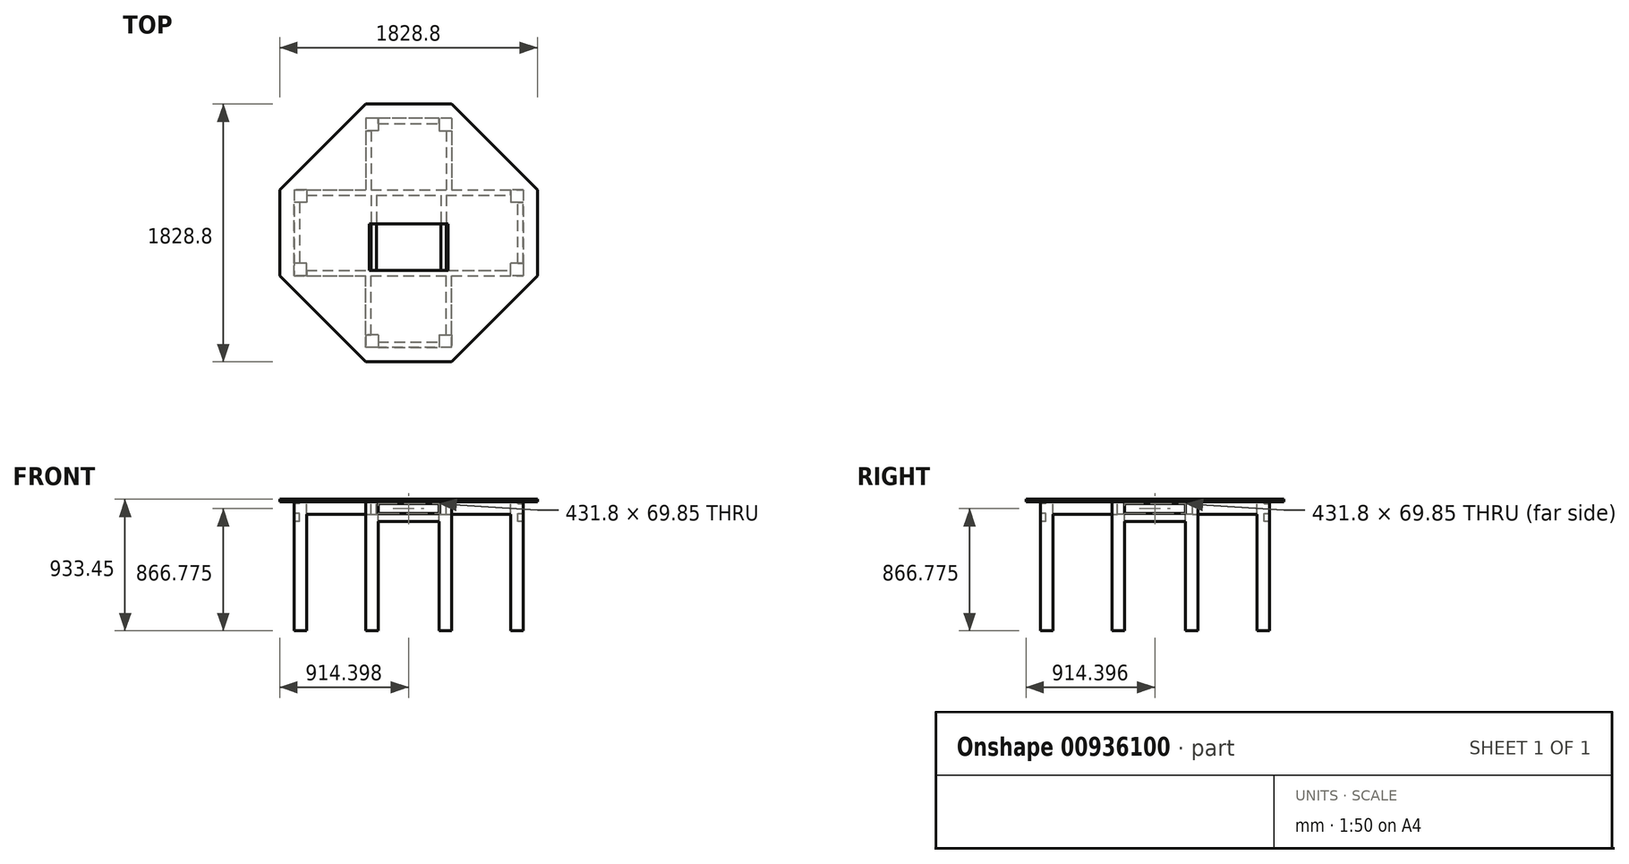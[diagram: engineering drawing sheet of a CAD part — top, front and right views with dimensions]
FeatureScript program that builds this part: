
annotation { "Feature Type Name" : "Feature", "Feature Type Description" : "" }
export const myFeature = defineFeature(function(context is Context, id is Id, definition is map)
    precondition{}
    {
        {
            var Q0;
            Q0=qCreatedBy(makeId("Top.planeOp"),FACE);
            var sketch = newSketch(context, id + "F0", { "sketchPlane" : qUnion([Q0])});
            skLineSegment(sketch, "E0.bottom", {"start": v(-298, -538.32) * mm, "end": v(311.6, -538.32) * mm});
            skLineSegment(sketch, "E0.top", {"start": v(-298, 1290.48) * mm, "end": v(311.6, 1290.48) * mm});
            skLineSegment(sketch, "E0.left", {"start": v(-907.6, 71.28) * mm, "end": v(-907.6, 680.88) * mm});
            skLineSegment(sketch, "E0.right", {"start": v(921.2, 71.28) * mm, "end": v(921.2, 680.88) * mm});
            skLineSegment(sketch, "E1", {"start": v(-298, -538.32) * mm, "end": v(-907.6, 71.28) * mm});
            skLineSegment(sketch, "E2", {"start": v(-907.6, 680.88) * mm, "end": v(-298, 1290.48) * mm});
            skLineSegment(sketch, "E3", {"start": v(921.2, 680.88) * mm, "end": v(311.6, 1290.48) * mm});
            skLineSegment(sketch, "E4", {"start": v(921.2, 71.28) * mm, "end": v(311.6, -538.32) * mm});
            skLineSegment(sketch, "E5.bottom", {"start": v(-272.6, 109.38) * mm, "end": v(286.2, 109.38) * mm});
            skLineSegment(sketch, "E5.top", {"start": v(-272.6, 439.58) * mm, "end": v(286.2, 439.58) * mm});
            skLineSegment(sketch, "E5.left", {"start": v(-272.6, 109.38) * mm, "end": v(-272.6, 439.58) * mm});
            skLineSegment(sketch, "E5.right", {"start": v(286.2, 109.38) * mm, "end": v(286.2, 439.58) * mm});
            skSolve(sketch);
        }
        {
            var Q0;
            Q0=makeQuery(id+"F0.imprint","IMPRINT",FACE,{"disambiguationData":[TD([[makeQuery(id+"F0.imprint","IMPRINT",EDGE,{"derivedFrom":sQuery(id+"F0.wireOp",EDGE,"E0.bottom")}),1.0]])]});
            extrude(context, id + "F1", {"entities" : qUnion([Q0]), "depth" : 19.05 * mm, "offsetDistance" : 25.4 * mm});
        }
        {
            var Q0;
            Q0=makeQuery(id+"F1.opExtrude","CAP_FACE",FACE,{"disambiguationData":[OSD([sQuery(id+"F0.wireOp",EDGE,"E0.bottom"),sQuery(id+"F0.wireOp",EDGE,"E0.top"),sQuery(id+"F0.wireOp",EDGE,"E0.left"),sQuery(id+"F0.wireOp",EDGE,"E0.right"),sQuery(id+"F0.wireOp",EDGE,"E1"),sQuery(id+"F0.wireOp",EDGE,"E2"),sQuery(id+"F0.wireOp",EDGE,"E3"),sQuery(id+"F0.wireOp",EDGE,"E4"),sQuery(id+"F0.wireOp",EDGE,"E5.bottom"),sQuery(id+"F0.wireOp",EDGE,"E5.top"),sQuery(id+"F0.wireOp",EDGE,"E5.left"),sQuery(id+"F0.wireOp",EDGE,"E5.right")])],"isStart":true});
            var sketch = newSketch(context, id + "F2", { "sketchPlane" : qUnion([Q0])});
            skLineSegment(sketch, "E6.bottom", {"start": v(-806, -680.88) * mm, "end": v(-717.1, -680.88) * mm});
            skLineSegment(sketch, "E6.top", {"start": v(-806, -591.98) * mm, "end": v(-717.1, -591.98) * mm});
            skLineSegment(sketch, "E6.left", {"start": v(-806, -680.88) * mm, "end": v(-806, -591.98) * mm});
            skLineSegment(sketch, "E6.right", {"start": v(-717.1, -680.88) * mm, "end": v(-717.1, -591.98) * mm});
            skLineSegment(sketch, "E7.bottom", {"start": v(-806, -160.18) * mm, "end": v(-717.1, -160.18) * mm});
            skLineSegment(sketch, "E7.top", {"start": v(-806, -71.28) * mm, "end": v(-717.1, -71.28) * mm});
            skLineSegment(sketch, "E7.left", {"start": v(-806, -160.18) * mm, "end": v(-806, -71.28) * mm});
            skLineSegment(sketch, "E7.right", {"start": v(-717.1, -160.18) * mm, "end": v(-717.1, -71.28) * mm});
            skLineSegment(sketch, "E8.bottom", {"start": v(-298, 436.72) * mm, "end": v(-209.1, 436.72) * mm});
            skLineSegment(sketch, "E8.top", {"start": v(-298, 347.82) * mm, "end": v(-209.1, 347.82) * mm});
            skLineSegment(sketch, "E8.left", {"start": v(-298, 436.72) * mm, "end": v(-298, 347.82) * mm});
            skLineSegment(sketch, "E8.right", {"start": v(-209.1, 436.72) * mm, "end": v(-209.1, 347.82) * mm});
            skLineSegment(sketch, "E9.bottom", {"start": v(222.7, 436.72) * mm, "end": v(311.6, 436.72) * mm});
            skLineSegment(sketch, "E9.top", {"start": v(222.7, 347.82) * mm, "end": v(311.6, 347.82) * mm});
            skLineSegment(sketch, "E9.left", {"start": v(222.7, 436.72) * mm, "end": v(222.7, 347.82) * mm});
            skLineSegment(sketch, "E9.right", {"start": v(311.6, 436.72) * mm, "end": v(311.6, 347.82) * mm});
            skLineSegment(sketch, "E10.bottom", {"start": v(730.7, -71.28) * mm, "end": v(819.6, -71.28) * mm});
            skLineSegment(sketch, "E10.top", {"start": v(730.7, -160.18) * mm, "end": v(819.6, -160.18) * mm});
            skLineSegment(sketch, "E10.left", {"start": v(730.7, -71.28) * mm, "end": v(730.7, -160.18) * mm});
            skLineSegment(sketch, "E10.right", {"start": v(819.6, -71.28) * mm, "end": v(819.6, -160.18) * mm});
            skPoint(sketch, "E11.firstSnap0", {"position": v(730.7, -115.73) * mm});
            skLineSegment(sketch, "E11.bottom", {"start": v(730.7, -591.98) * mm, "end": v(819.6, -591.98) * mm});
            skLineSegment(sketch, "E11.top", {"start": v(730.7, -680.88) * mm, "end": v(819.6, -680.88) * mm});
            skLineSegment(sketch, "E11.left", {"start": v(730.7, -591.98) * mm, "end": v(730.7, -680.88) * mm});
            skLineSegment(sketch, "E11.right", {"start": v(819.6, -591.98) * mm, "end": v(819.6, -680.88) * mm});
            skLineSegment(sketch, "E12.bottom", {"start": v(222.7, -1099.98) * mm, "end": v(311.6, -1099.98) * mm});
            skLineSegment(sketch, "E12.top", {"start": v(222.7, -1188.88) * mm, "end": v(311.6, -1188.88) * mm});
            skLineSegment(sketch, "E12.left", {"start": v(222.7, -1099.98) * mm, "end": v(222.7, -1188.88) * mm});
            skLineSegment(sketch, "E12.right", {"start": v(311.6, -1099.98) * mm, "end": v(311.6, -1188.88) * mm});
            skLineSegment(sketch, "E13.bottom", {"start": v(-298, -1099.98) * mm, "end": v(-209.1, -1099.98) * mm});
            skLineSegment(sketch, "E13.top", {"start": v(-298, -1188.88) * mm, "end": v(-209.1, -1188.88) * mm});
            skLineSegment(sketch, "E13.left", {"start": v(-298, -1099.98) * mm, "end": v(-298, -1188.88) * mm});
            skLineSegment(sketch, "E13.right", {"start": v(-209.1, -1099.98) * mm, "end": v(-209.1, -1188.88) * mm});
            skLineSegment(sketch, "E14.bottom", {"start": v(-209.1, 436.72) * mm, "end": v(222.7, 436.72) * mm});
            skLineSegment(sketch, "E14.top", {"start": v(-209.1, 398.62) * mm, "end": v(222.7, 398.62) * mm});
            skLineSegment(sketch, "E14.left", {"start": v(-209.1, 436.72) * mm, "end": v(-209.1, 398.62) * mm});
            skLineSegment(sketch, "E14.right", {"start": v(222.7, 436.72) * mm, "end": v(222.7, 398.62) * mm});
            skLineSegment(sketch, "E15.bottom", {"start": v(-806, -160.18) * mm, "end": v(-767.9, -160.18) * mm});
            skLineSegment(sketch, "E15.top", {"start": v(-806, -591.98) * mm, "end": v(-767.9, -591.98) * mm});
            skLineSegment(sketch, "E15.left", {"start": v(-806, -160.18) * mm, "end": v(-806, -591.98) * mm});
            skLineSegment(sketch, "E15.right", {"start": v(-767.9, -160.18) * mm, "end": v(-767.9, -591.98) * mm});
            skLineSegment(sketch, "E16.bottom", {"start": v(-209.1, -1188.88) * mm, "end": v(222.7, -1188.88) * mm});
            skLineSegment(sketch, "E16.top", {"start": v(-209.1, -1150.78) * mm, "end": v(222.7, -1150.78) * mm});
            skLineSegment(sketch, "E16.left", {"start": v(-209.1, -1188.88) * mm, "end": v(-209.1, -1150.78) * mm});
            skLineSegment(sketch, "E16.right", {"start": v(222.7, -1188.88) * mm, "end": v(222.7, -1150.78) * mm});
            skLineSegment(sketch, "E17.bottom", {"start": v(819.6, -160.18) * mm, "end": v(781.5, -160.18) * mm});
            skLineSegment(sketch, "E17.top", {"start": v(819.6, -591.98) * mm, "end": v(781.5, -591.98) * mm});
            skLineSegment(sketch, "E17.left", {"start": v(819.6, -160.18) * mm, "end": v(819.6, -591.98) * mm});
            skLineSegment(sketch, "E17.right", {"start": v(781.5, -160.18) * mm, "end": v(781.5, -591.98) * mm});
            skLineSegment(sketch, "E18.bottom", {"start": v(-717.1, -71.28) * mm, "end": v(730.7, -71.28) * mm});
            skLineSegment(sketch, "E18.top", {"start": v(-717.1, -109.38) * mm, "end": v(730.7, -109.38) * mm});
            skLineSegment(sketch, "E18.left", {"start": v(-717.1, -71.28) * mm, "end": v(-717.1, -109.38) * mm});
            skLineSegment(sketch, "E18.right", {"start": v(730.7, -71.28) * mm, "end": v(730.7, -109.38) * mm});
            skLineSegment(sketch, "E19.bottom", {"start": v(-717.1, -680.88) * mm, "end": v(730.7, -680.88) * mm});
            skLineSegment(sketch, "E19.top", {"start": v(-717.1, -642.78) * mm, "end": v(730.7, -642.78) * mm});
            skLineSegment(sketch, "E19.left", {"start": v(-717.1, -680.88) * mm, "end": v(-717.1, -642.78) * mm});
            skLineSegment(sketch, "E19.right", {"start": v(730.7, -680.88) * mm, "end": v(730.7, -642.78) * mm});
            skLineSegment(sketch, "E20.bottom", {"start": v(311.6, 347.82) * mm, "end": v(273.5, 347.82) * mm});
            skLineSegment(sketch, "E20.top", {"start": v(311.6, -71.28) * mm, "end": v(273.5, -71.28) * mm});
            skLineSegment(sketch, "E20.left", {"start": v(311.6, 347.82) * mm, "end": v(311.6, -71.28) * mm});
            skLineSegment(sketch, "E20.right", {"start": v(273.5, 347.82) * mm, "end": v(273.5, -71.28) * mm});
            skLineSegment(sketch, "E21.bottom", {"start": v(-298, 347.82) * mm, "end": v(-259.9, 347.82) * mm});
            skLineSegment(sketch, "E21.top", {"start": v(-298, -71.28) * mm, "end": v(-259.9, -71.28) * mm});
            skLineSegment(sketch, "E21.left", {"start": v(-298, 347.82) * mm, "end": v(-298, -71.28) * mm});
            skLineSegment(sketch, "E21.right", {"start": v(-259.9, 347.82) * mm, "end": v(-259.9, -71.28) * mm});
            skLineSegment(sketch, "E22.bottom", {"start": v(-298, -1099.98) * mm, "end": v(-259.9, -1099.98) * mm});
            skLineSegment(sketch, "E22.top", {"start": v(-298, -680.88) * mm, "end": v(-259.9, -680.88) * mm});
            skLineSegment(sketch, "E22.left", {"start": v(-298, -1099.98) * mm, "end": v(-298, -680.88) * mm});
            skLineSegment(sketch, "E22.right", {"start": v(-259.9, -1099.98) * mm, "end": v(-259.9, -680.88) * mm});
            skLineSegment(sketch, "E23.bottom", {"start": v(311.6, -1099.98) * mm, "end": v(273.5, -1099.98) * mm});
            skLineSegment(sketch, "E23.top", {"start": v(311.6, -680.88) * mm, "end": v(273.5, -680.88) * mm});
            skLineSegment(sketch, "E23.left", {"start": v(311.6, -1099.98) * mm, "end": v(311.6, -680.88) * mm});
            skLineSegment(sketch, "E23.right", {"start": v(273.5, -1099.98) * mm, "end": v(273.5, -680.88) * mm});
            skLineSegment(sketch, "E24.bottom", {"start": v(273.5, -642.78) * mm, "end": v(235.4, -642.78) * mm});
            skLineSegment(sketch, "E24.top", {"start": v(273.5, -109.38) * mm, "end": v(235.4, -109.38) * mm});
            skLineSegment(sketch, "E24.left", {"start": v(273.5, -642.78) * mm, "end": v(273.5, -109.38) * mm});
            skLineSegment(sketch, "E24.right", {"start": v(235.4, -642.78) * mm, "end": v(235.4, -109.38) * mm});
            skLineSegment(sketch, "E25.bottom", {"start": v(-259.9, -642.78) * mm, "end": v(-221.8, -642.78) * mm});
            skLineSegment(sketch, "E25.top", {"start": v(-259.9, -109.38) * mm, "end": v(-221.8, -109.38) * mm});
            skLineSegment(sketch, "E25.left", {"start": v(-259.9, -642.78) * mm, "end": v(-259.9, -109.38) * mm});
            skLineSegment(sketch, "E25.right", {"start": v(-221.8, -642.78) * mm, "end": v(-221.8, -109.38) * mm});
            skSolve(sketch);
        }
        {
            var Q0;
            {var subQ2=sQuery(id+"F2.wireOp",EDGE,"E22.left");Q0=makeQuery(id+"F2.imprint","IMPRINT",FACE,{"disambiguationData":[TD([[makeQuery(id+"F2.imprint","IMPRINT",EDGE,{"derivedFrom":subQ2}),-1.0]])]});}
            var Q1;
            {var subQ0=sQuery(id+"F2.wireOp",EDGE,"E23.left");Q1=makeQuery(id+"F2.imprint","IMPRINT",FACE,{"disambiguationData":[TD([[makeQuery(id+"F2.imprint","IMPRINT",EDGE,{"derivedFrom":subQ0}),1.0]])]});}
            var Q2;
            {var subQ7=sQuery(id+"F2.wireOp",EDGE,"E19.bottom");var subQ14=makeQuery(id+"F2.imprint","INTERSECT",VERTEX,{"derivedFrom":[subQ7,sQuery(id+"F2.wireOp",EDGE,"E22.right")]});Q2=makeQuery(id+"F2.imprint","IMPRINT",FACE,{"disambiguationData":[TD([[makeQuery(id+"F2.imprint","IMPRINT",EDGE,{"disambiguationData":[TD([[subQ14,-1.0]])],"derivedFrom":subQ7}),1.0]])]});}
            var Q3;
            {var subQ0=sQuery(id+"F2.wireOp",EDGE,"E25.right");var subQ1=sQuery(id+"F2.wireOp",EDGE,"E19.top");var subQ2=makeQuery(id+"F2.imprint","INTERSECT",VERTEX,{"derivedFrom":[subQ1,subQ0]});Q3=makeQuery(id+"F2.imprint","IMPRINT",FACE,{"disambiguationData":[TD([[makeQuery(id+"F2.imprint","IMPRINT",EDGE,{"disambiguationData":[TD([[subQ2,1.0]])],"derivedFrom":subQ1}),1.0]])]});}
            var Q4;
            {var subQ4=sQuery(id+"F2.wireOp",EDGE,"E18.bottom");var subQ7=makeQuery(id+"F2.imprint","INTERSECT",VERTEX,{"derivedFrom":[subQ4,sQuery(id+"F2.wireOp",EDGE,"E21.right")]});Q4=makeQuery(id+"F2.imprint","IMPRINT",FACE,{"disambiguationData":[TD([[makeQuery(id+"F2.imprint","IMPRINT",EDGE,{"disambiguationData":[TD([[subQ7,-1.0]])],"derivedFrom":subQ4}),-1.0]])]});}
            var Q5;
            {var subQ2=sQuery(id+"F2.wireOp",EDGE,"E21.left");Q5=makeQuery(id+"F2.imprint","IMPRINT",FACE,{"disambiguationData":[TD([[makeQuery(id+"F2.imprint","IMPRINT",EDGE,{"derivedFrom":subQ2}),1.0]])]});}
            var Q6;
            {var subQ0=sQuery(id+"F2.wireOp",EDGE,"E20.left");Q6=makeQuery(id+"F2.imprint","IMPRINT",FACE,{"disambiguationData":[TD([[makeQuery(id+"F2.imprint","IMPRINT",EDGE,{"derivedFrom":subQ0}),-1.0]])]});}
            var Q7;
            {var subQ0=sQuery(id+"F2.wireOp",EDGE,"E24.left");var subQ1=sQuery(id+"F2.wireOp",EDGE,"E19.top");var subQ2=makeQuery(id+"F2.imprint","INTERSECT",VERTEX,{"derivedFrom":[subQ1,subQ0]});Q7=makeQuery(id+"F2.imprint","IMPRINT",FACE,{"disambiguationData":[TD([[makeQuery(id+"F2.imprint","IMPRINT",EDGE,{"disambiguationData":[TD([[subQ2,1.0]])],"derivedFrom":subQ1}),1.0]])]});}
            var Q8;
            {var subQ0=sQuery(id+"F2.wireOp",EDGE,"E25.left");var subQ1=sQuery(id+"F2.wireOp",EDGE,"E18.top");var subQ2=makeQuery(id+"F2.imprint","INTERSECT",VERTEX,{"derivedFrom":[subQ1,subQ0]});Q8=makeQuery(id+"F2.imprint","IMPRINT",FACE,{"disambiguationData":[TD([[makeQuery(id+"F2.imprint","IMPRINT",EDGE,{"disambiguationData":[TD([[subQ2,-1.0]])],"derivedFrom":subQ1}),-1.0]])]});}
            var Q9;
            {var subQ0=sQuery(id+"F2.wireOp",EDGE,"E24.left");var subQ1=sQuery(id+"F2.wireOp",EDGE,"E18.top");var subQ2=makeQuery(id+"F2.imprint","INTERSECT",VERTEX,{"derivedFrom":[subQ1,subQ0]});Q9=makeQuery(id+"F2.imprint","IMPRINT",FACE,{"disambiguationData":[TD([[makeQuery(id+"F2.imprint","IMPRINT",EDGE,{"disambiguationData":[TD([[subQ2,1.0]])],"derivedFrom":subQ1}),-1.0]])]});}
            extrude(context, id + "F3", {"entities" : qUnion([Q0, Q1, Q2, Q3, Q4, Q5, Q6, Q7, Q8, Q9]), "operationType" : NewBodyOperationType.ADD, "depth" : 88.9 * mm, "offsetDistance" : 25.4 * mm});
        }
        {
            var Q0;
            {var subQ5=sQuery(id+"F0.wireOp",EDGE,"E5.right");var subQ8=sQuery(id+"F0.wireOp",EDGE,"E5.left");var subQ12=sQuery(id+"F0.wireOp",EDGE,"E0.left");var subQ14=sQuery(id+"F0.wireOp",EDGE,"E0.top");var subQ30=sQuery(id+"F0.wireOp",EDGE,"E0.right");var subQ31=sQuery(id+"F0.wireOp",EDGE,"E0.bottom");var subQ34=sQuery(id+"F0.wireOp",EDGE,"E5.top");var subQ35=sQuery(id+"F0.wireOp",EDGE,"E1");var subQ37=sQuery(id+"F0.wireOp",EDGE,"E2");var subQ38=sQuery(id+"F0.wireOp",EDGE,"E3");var subQ41=sQuery(id+"F0.wireOp",EDGE,"E4");var subQ42=sQuery(id+"F0.wireOp",EDGE,"E5.bottom");Q0=makeQuery(id+"F3.boolean.opBoolean","SPLIT",FACE,{"disambiguationData":[TD([makeQuery(id+"F1.opExtrude","SWEPT_FACE",FACE,{"disambiguationData":[OSD([subQ31])]})])],"derivedFrom":makeQuery(id+"F1.opExtrude","CAP_FACE",FACE,{"disambiguationData":[OSD([subQ31,subQ14,subQ12,subQ30,subQ35,subQ37,subQ38,subQ41,subQ42,subQ34,subQ8,subQ5])],"isStart":true})});}
            var sketch = newSketch(context, id + "F4", { "sketchPlane" : qUnion([Q0])});
            skLineSegment(sketch, "E26.bottom", {"start": v(819.6, -680.88) * mm, "end": v(730.7, -680.88) * mm});
            skLineSegment(sketch, "E26.top", {"start": v(819.6, -591.98) * mm, "end": v(730.7, -591.98) * mm});
            skLineSegment(sketch, "E26.left", {"start": v(819.6, -680.88) * mm, "end": v(819.6, -591.98) * mm});
            skLineSegment(sketch, "E26.right", {"start": v(730.7, -680.88) * mm, "end": v(730.7, -591.98) * mm});
            skLineSegment(sketch, "E27.bottom", {"start": v(819.6, -160.18) * mm, "end": v(730.7, -160.18) * mm});
            skLineSegment(sketch, "E27.top", {"start": v(819.6, -71.28) * mm, "end": v(730.7, -71.28) * mm});
            skLineSegment(sketch, "E27.left", {"start": v(819.6, -160.18) * mm, "end": v(819.6, -71.28) * mm});
            skLineSegment(sketch, "E27.right", {"start": v(730.7, -160.18) * mm, "end": v(730.7, -71.28) * mm});
            skLineSegment(sketch, "E28.bottom", {"start": v(311.6, -1188.88) * mm, "end": v(222.7, -1188.88) * mm});
            skLineSegment(sketch, "E28.top", {"start": v(311.6, -1099.98) * mm, "end": v(222.7, -1099.98) * mm});
            skLineSegment(sketch, "E28.left", {"start": v(311.6, -1188.88) * mm, "end": v(311.6, -1099.98) * mm});
            skLineSegment(sketch, "E28.right", {"start": v(222.7, -1188.88) * mm, "end": v(222.7, -1099.98) * mm});
            skLineSegment(sketch, "E29.bottom", {"start": v(-717.1, -680.88) * mm, "end": v(-806, -680.88) * mm});
            skLineSegment(sketch, "E29.top", {"start": v(-717.1, -591.98) * mm, "end": v(-806, -591.98) * mm});
            skLineSegment(sketch, "E29.left", {"start": v(-717.1, -680.88) * mm, "end": v(-717.1, -591.98) * mm});
            skLineSegment(sketch, "E29.right", {"start": v(-806, -680.88) * mm, "end": v(-806, -591.98) * mm});
            skLineSegment(sketch, "E30.bottom", {"start": v(-209.1, -1188.88) * mm, "end": v(-298, -1188.88) * mm});
            skLineSegment(sketch, "E30.top", {"start": v(-209.1, -1099.98) * mm, "end": v(-298, -1099.98) * mm});
            skLineSegment(sketch, "E30.left", {"start": v(-209.1, -1188.88) * mm, "end": v(-209.1, -1099.98) * mm});
            skLineSegment(sketch, "E30.right", {"start": v(-298, -1188.88) * mm, "end": v(-298, -1099.98) * mm});
            skLineSegment(sketch, "E31.bottom", {"start": v(311.6, 347.82) * mm, "end": v(222.7, 347.82) * mm});
            skLineSegment(sketch, "E31.top", {"start": v(311.6, 436.72) * mm, "end": v(222.7, 436.72) * mm});
            skLineSegment(sketch, "E31.left", {"start": v(311.6, 347.82) * mm, "end": v(311.6, 436.72) * mm});
            skLineSegment(sketch, "E31.right", {"start": v(222.7, 347.82) * mm, "end": v(222.7, 436.72) * mm});
            skLineSegment(sketch, "E32.bottom", {"start": v(-209.1, 347.82) * mm, "end": v(-298, 347.82) * mm});
            skLineSegment(sketch, "E32.top", {"start": v(-209.1, 436.72) * mm, "end": v(-298, 436.72) * mm});
            skLineSegment(sketch, "E32.left", {"start": v(-209.1, 347.82) * mm, "end": v(-209.1, 436.72) * mm});
            skLineSegment(sketch, "E32.right", {"start": v(-298, 347.82) * mm, "end": v(-298, 436.72) * mm});
            skLineSegment(sketch, "E33.bottom", {"start": v(-717.1, -71.28) * mm, "end": v(-806, -71.28) * mm});
            skLineSegment(sketch, "E33.top", {"start": v(-717.1, -160.18) * mm, "end": v(-806, -160.18) * mm});
            skLineSegment(sketch, "E33.left", {"start": v(-717.1, -71.28) * mm, "end": v(-717.1, -160.18) * mm});
            skLineSegment(sketch, "E33.right", {"start": v(-806, -71.28) * mm, "end": v(-806, -160.18) * mm});
            skSolve(sketch);
        }
        {
            var Q0;
            Q0 = qSketchRegion(id + "F4", true);
            extrude(context, id + "F5", {"entities" : qUnion([Q0]), "operationType" : NewBodyOperationType.ADD, "depth" : 914.4 * mm, "offsetDistance" : 25.4 * mm});
        }
        {
            var Q0;
            {var subQ5=sQuery(id+"F0.wireOp",EDGE,"E5.right");var subQ8=sQuery(id+"F0.wireOp",EDGE,"E5.left");var subQ12=sQuery(id+"F0.wireOp",EDGE,"E0.left");var subQ14=sQuery(id+"F0.wireOp",EDGE,"E0.top");var subQ30=sQuery(id+"F0.wireOp",EDGE,"E0.right");var subQ31=sQuery(id+"F0.wireOp",EDGE,"E0.bottom");var subQ34=sQuery(id+"F0.wireOp",EDGE,"E5.top");var subQ35=sQuery(id+"F0.wireOp",EDGE,"E1");var subQ37=sQuery(id+"F0.wireOp",EDGE,"E2");var subQ38=sQuery(id+"F0.wireOp",EDGE,"E3");var subQ41=sQuery(id+"F0.wireOp",EDGE,"E4");var subQ42=sQuery(id+"F0.wireOp",EDGE,"E5.bottom");Q0=makeQuery(id+"F3.boolean.opBoolean","SPLIT",FACE,{"disambiguationData":[TD([makeQuery(id+"F1.opExtrude","SWEPT_FACE",FACE,{"disambiguationData":[OSD([subQ31])]})])],"derivedFrom":makeQuery(id+"F1.opExtrude","CAP_FACE",FACE,{"disambiguationData":[OSD([subQ31,subQ14,subQ12,subQ30,subQ35,subQ37,subQ38,subQ41,subQ42,subQ34,subQ8,subQ5])],"isStart":true})});}
            var sketch = newSketch(context, id + "F6", { "sketchPlane" : qUnion([Q0])});
            skLineSegment(sketch, "E34.bottom", {"start": v(819.6, -160.18) * mm, "end": v(781.5, -160.18) * mm});
            skLineSegment(sketch, "E34.top", {"start": v(819.6, -591.98) * mm, "end": v(781.5, -591.98) * mm});
            skLineSegment(sketch, "E34.left", {"start": v(819.6, -160.18) * mm, "end": v(819.6, -591.98) * mm});
            skLineSegment(sketch, "E34.right", {"start": v(781.5, -160.18) * mm, "end": v(781.5, -591.98) * mm});
            skLineSegment(sketch, "E35.bottom", {"start": v(-767.9, -160.18) * mm, "end": v(-806, -160.18) * mm});
            skLineSegment(sketch, "E35.top", {"start": v(-767.9, -591.98) * mm, "end": v(-806, -591.98) * mm});
            skLineSegment(sketch, "E35.left", {"start": v(-767.9, -160.18) * mm, "end": v(-767.9, -591.98) * mm});
            skLineSegment(sketch, "E35.right", {"start": v(-806, -160.18) * mm, "end": v(-806, -591.98) * mm});
            skLineSegment(sketch, "E36.bottom", {"start": v(222.7, -1188.88) * mm, "end": v(-209.1, -1188.88) * mm});
            skLineSegment(sketch, "E36.top", {"start": v(222.7, -1150.78) * mm, "end": v(-209.1, -1150.78) * mm});
            skLineSegment(sketch, "E36.left", {"start": v(222.7, -1188.88) * mm, "end": v(222.7, -1150.78) * mm});
            skLineSegment(sketch, "E36.right", {"start": v(-209.1, -1188.88) * mm, "end": v(-209.1, -1150.78) * mm});
            skLineSegment(sketch, "E37.bottom", {"start": v(-209.1, 436.72) * mm, "end": v(222.7, 436.72) * mm});
            skLineSegment(sketch, "E37.top", {"start": v(-209.1, 398.62) * mm, "end": v(222.7, 398.62) * mm});
            skLineSegment(sketch, "E37.left", {"start": v(-209.1, 436.72) * mm, "end": v(-209.1, 398.62) * mm});
            skLineSegment(sketch, "E37.right", {"start": v(222.7, 436.72) * mm, "end": v(222.7, 398.62) * mm});
            skSolve(sketch);
        }
        {
            var Q0;
            Q0 = qSketchRegion(id + "F6", true);
            extrude(context, id + "F7", {"entities" : qUnion([Q0]), "operationType" : NewBodyOperationType.ADD, "depth" : 139.7 * mm, "offsetDistance" : 25.4 * mm});
        }
        {
            var Q0;
            Q0=makeQuery(id+"F7.boolean.opBoolean","MERGE",FACE,{"derivedFrom":[makeQuery(id+"F5.opExtrude","SWEPT_FACE",FACE,{"disambiguationData":[OSD([sQuery(id+"F4.wireOp",EDGE,"E31.top")])]}),makeQuery(id+"F5.opExtrude","SWEPT_FACE",FACE,{"disambiguationData":[OSD([sQuery(id+"F4.wireOp",EDGE,"E32.top")])]}),makeQuery(id+"F7.opExtrude","SWEPT_FACE",FACE,{"disambiguationData":[OSD([sQuery(id+"F6.wireOp",EDGE,"E37.bottom")])]})]});
            var sketch = newSketch(context, id + "F8", { "sketchPlane" : qUnion([Q0])});
            skLineSegment(sketch, "E38.bottom", {"start": v(-209.1, -12.7) * mm, "end": v(222.7, -12.7) * mm});
            skLineSegment(sketch, "E38.top", {"start": v(-209.1, -82.55) * mm, "end": v(222.7, -82.55) * mm});
            skLineSegment(sketch, "E38.left", {"start": v(-209.1, -12.7) * mm, "end": v(-209.1, -82.55) * mm});
            skLineSegment(sketch, "E38.right", {"start": v(222.7, -12.7) * mm, "end": v(222.7, -82.55) * mm});
            skSolve(sketch);
        }
        {
            var Q0;
            Q0 = qSketchRegion(id + "F8", true);
            extrude(context, id + "F9", {"entities" : qUnion([Q0]), "operationType" : NewBodyOperationType.REMOVE, "oppositeDirection" : true, "depth" : 78.74 * mm, "offsetDistance" : 25.4 * mm});
        }
        {
            var Q0;
            Q0=makeQuery(id+"F7.boolean.opBoolean","MERGE",FACE,{"derivedFrom":[makeQuery(id+"F5.opExtrude","SWEPT_FACE",FACE,{"disambiguationData":[OSD([sQuery(id+"F4.wireOp",EDGE,"E29.right")])]}),makeQuery(id+"F5.opExtrude","SWEPT_FACE",FACE,{"disambiguationData":[OSD([sQuery(id+"F4.wireOp",EDGE,"E33.right")])]}),makeQuery(id+"F7.opExtrude","SWEPT_FACE",FACE,{"disambiguationData":[OSD([sQuery(id+"F6.wireOp",EDGE,"E35.right")])]})]});
            var sketch = newSketch(context, id + "F10", { "sketchPlane" : qUnion([Q0])});
            skLineSegment(sketch, "E39.bottom", {"start": v(-160.18, -82.55) * mm, "end": v(-591.98, -82.55) * mm});
            skLineSegment(sketch, "E39.top", {"start": v(-160.18, -12.7) * mm, "end": v(-591.98, -12.7) * mm});
            skLineSegment(sketch, "E39.left", {"start": v(-160.18, -82.55) * mm, "end": v(-160.18, -12.7) * mm});
            skLineSegment(sketch, "E39.right", {"start": v(-591.98, -82.55) * mm, "end": v(-591.98, -12.7) * mm});
            skSolve(sketch);
        }
        {
            var Q0;
            Q0 = qSketchRegion(id + "F10", true);
            extrude(context, id + "F11", {"entities" : qUnion([Q0]), "operationType" : NewBodyOperationType.REMOVE, "oppositeDirection" : true, "depth" : 66.04 * mm, "offsetDistance" : 25.4 * mm});
        }
        {
            var Q0;
            Q0=makeQuery(id+"F7.boolean.opBoolean","MERGE",FACE,{"derivedFrom":[makeQuery(id+"F5.opExtrude","SWEPT_FACE",FACE,{"disambiguationData":[OSD([sQuery(id+"F4.wireOp",EDGE,"E26.left")])]}),makeQuery(id+"F5.opExtrude","SWEPT_FACE",FACE,{"disambiguationData":[OSD([sQuery(id+"F4.wireOp",EDGE,"E27.left")])]}),makeQuery(id+"F7.opExtrude","SWEPT_FACE",FACE,{"disambiguationData":[OSD([sQuery(id+"F6.wireOp",EDGE,"E34.left")])]})]});
            var sketch = newSketch(context, id + "F12", { "sketchPlane" : qUnion([Q0])});
            skLineSegment(sketch, "E40.bottom", {"start": v(160.18, -82.55) * mm, "end": v(591.98, -82.55) * mm});
            skLineSegment(sketch, "E40.top", {"start": v(160.18, -12.7) * mm, "end": v(591.98, -12.7) * mm});
            skLineSegment(sketch, "E40.left", {"start": v(160.18, -82.55) * mm, "end": v(160.18, -12.7) * mm});
            skLineSegment(sketch, "E40.right", {"start": v(591.98, -82.55) * mm, "end": v(591.98, -12.7) * mm});
            skSolve(sketch);
        }
        {
            var Q0;
            Q0 = qSketchRegion(id + "F12", true);
            extrude(context, id + "F13", {"entities" : qUnion([Q0]), "operationType" : NewBodyOperationType.REMOVE, "oppositeDirection" : true, "depth" : 53.34 * mm, "offsetDistance" : 25.4 * mm});
        }
        {
            var Q0;
            Q0=makeQuery(id+"F7.boolean.opBoolean","MERGE",FACE,{"derivedFrom":[makeQuery(id+"F5.opExtrude","SWEPT_FACE",FACE,{"disambiguationData":[OSD([sQuery(id+"F4.wireOp",EDGE,"E28.bottom")])]}),makeQuery(id+"F5.opExtrude","SWEPT_FACE",FACE,{"disambiguationData":[OSD([sQuery(id+"F4.wireOp",EDGE,"E30.bottom")])]}),makeQuery(id+"F7.opExtrude","SWEPT_FACE",FACE,{"disambiguationData":[OSD([sQuery(id+"F6.wireOp",EDGE,"E36.bottom")])]})]});
            var sketch = newSketch(context, id + "F14", { "sketchPlane" : qUnion([Q0])});
            skLineSegment(sketch, "E41.bottom", {"start": v(209.1, -82.55) * mm, "end": v(-222.7, -82.55) * mm});
            skLineSegment(sketch, "E41.top", {"start": v(209.1, -12.7) * mm, "end": v(-222.7, -12.7) * mm});
            skLineSegment(sketch, "E41.left", {"start": v(209.1, -82.55) * mm, "end": v(209.1, -12.7) * mm});
            skLineSegment(sketch, "E41.right", {"start": v(-222.7, -82.55) * mm, "end": v(-222.7, -12.7) * mm});
            skSolve(sketch);
        }
        {
            var Q0;
            Q0 = qSketchRegion(id + "F14", true);
            extrude(context, id + "F15", {"entities" : qUnion([Q0]), "operationType" : NewBodyOperationType.REMOVE, "oppositeDirection" : true, "depth" : 76.2 * mm, "offsetDistance" : 25.4 * mm});
        }
    });
